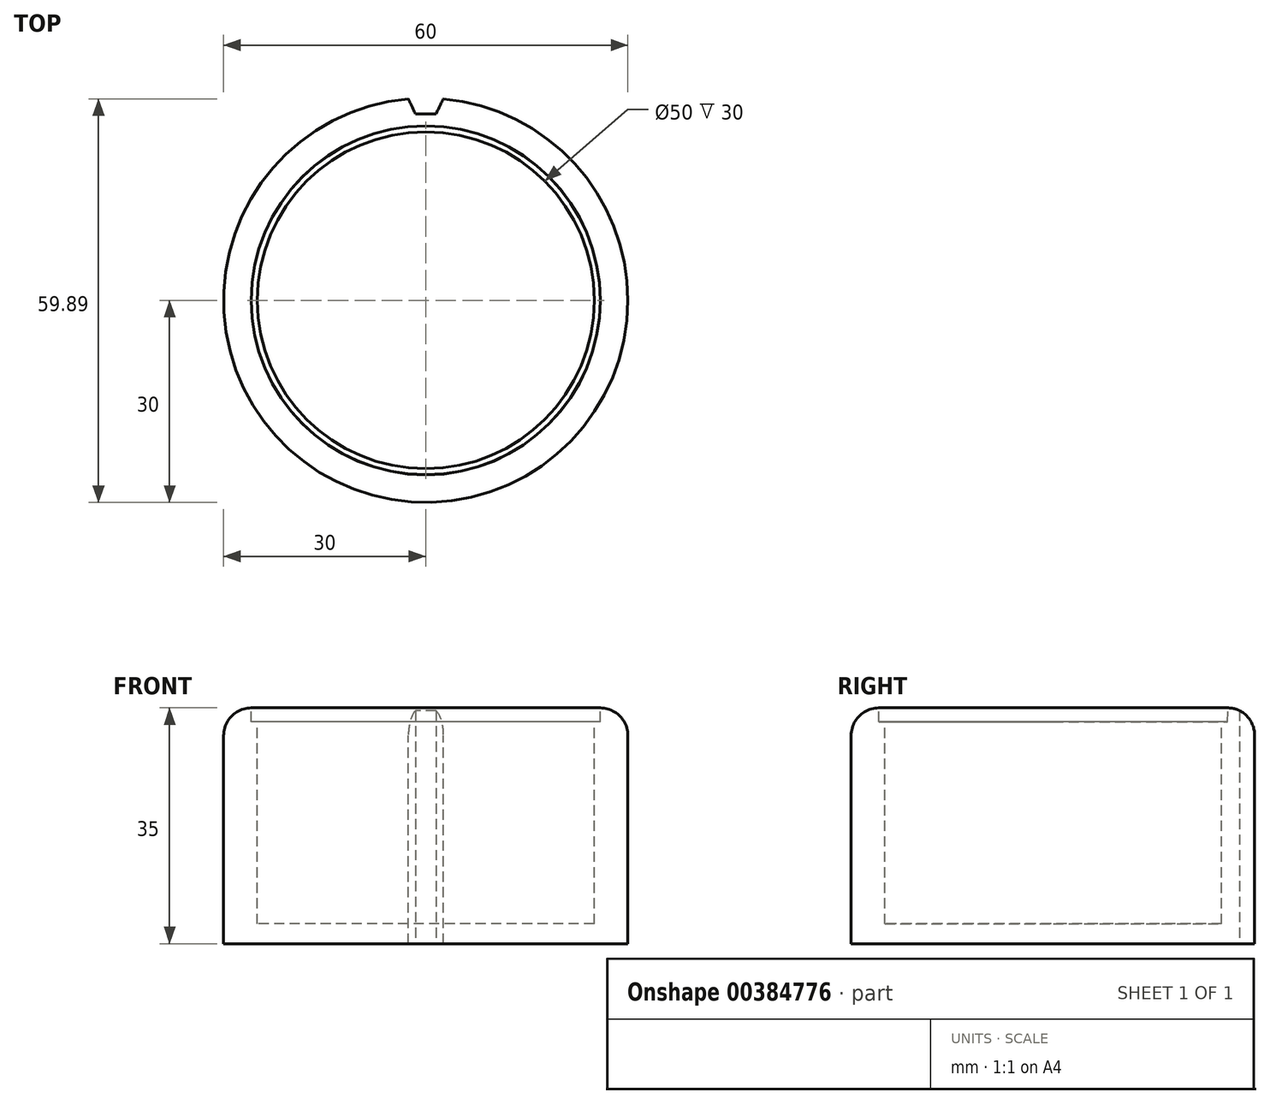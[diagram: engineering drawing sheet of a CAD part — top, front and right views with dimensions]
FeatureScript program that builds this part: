
annotation { "Feature Type Name" : "Feature", "Feature Type Description" : "" }
export const myFeature = defineFeature(function(context is Context, id is Id, definition is map)
    precondition{}
    {
        {
            var Q0;
            Q0=qCreatedBy(makeId("Front.planeOp"),FACE);
            var sketch = newSketch(context, id + "F0", { "sketchPlane" : qUnion([Q0])});
            skLineSegment(sketch, "E0", {"start": v(-30, 30.9) * mm, "end": v(-30, 0) * mm});
            skLineSegment(sketch, "E1", {"start": v(-30, 0) * mm, "end": v(0, 0) * mm});
            skLineSegment(sketch, "E2", {"start": v(0, 0) * mm, "end": v(0, 0) * mm});
            skLineSegment(sketch, "E3", {"start": v(-25, 32.94) * mm, "end": v(-25, 2.94) * mm});
            skLineSegment(sketch, "E4", {"start": v(-25, 2.94) * mm, "end": v(0, 2.94) * mm});
            skLineSegment(sketch, "E5", {"start": v(0, 2.94) * mm, "end": v(0, 0) * mm});
            skPoint(sketch, "E6.visualSharp", {"position": v(-30, 28.05) * mm});
            skArc(sketch, "E6.filletArc", {"start": v(-25.9, 35) * mm, "mid": v(-28.8, 33.8) * mm, "end": v(-30, 30.9) * mm});
            skLineSegment(sketch, "E7", {"start": v(-25.9, 32.94) * mm, "end": v(-25.9, 35) * mm});
            skLineSegment(sketch, "E8", {"start": v(-25.9, 32.94) * mm, "end": v(-25, 32.94) * mm});
            skSolve(sketch);
        }
        {
            var Q0;
            Q0=makeQuery(id+"F0.imprint","IMPRINT",FACE,{"disambiguationData":[TD([[makeQuery(id+"F0.imprint","IMPRINT",EDGE,{"derivedFrom":sQuery(id+"F0.wireOp",EDGE,"E0")}),1.0]])]});
            var Q1;
            Q1=sQuery(id+"F0.wireOp",EDGE,"E5");
            revolve(context, id + "F1", {"entities" : qUnion([Q0]), "axis" : qUnion([Q1]), "revolveType" : RevolveType.FULL});
        }
        {
            var Q0;
            Q0=qCreatedBy(makeId("Top.planeOp"),FACE);
            var sketch = newSketch(context, id + "F2", { "sketchPlane" : qUnion([Q0])});
            skLineSegment(sketch, "E9", {"start": v(-3.21, 31.22) * mm, "end": v(-1.52, 27.65) * mm});
            skLineSegment(sketch, "E10", {"start": v(-1.52, 27.65) * mm, "end": v(0, 27.65) * mm});
            skLineSegment(sketch, "E11.MirrorCS", {"start": v(3.21, 31.22) * mm, "end": v(1.52, 27.65) * mm});
            skLineSegment(sketch, "E12", {"start": v(1.52, 27.65) * mm, "end": v(0, 27.65) * mm});
            skPoint(sketch, "E13.start.orphan", {"position": v(0, 32) * mm});
            skLineSegment(sketch, "E14", {"start": v(3.21, 31.22) * mm, "end": v(-3.21, 31.22) * mm});
            skSolve(sketch);
        }
        {
            var Q0;
            Q0 = qSketchRegion(id + "F2", true);
            extrude(context, id + "F3", {"entities" : qUnion([Q0]), "operationType" : NewBodyOperationType.REMOVE, "depth" : 40 * mm});
        }
    });
